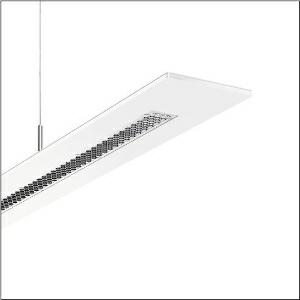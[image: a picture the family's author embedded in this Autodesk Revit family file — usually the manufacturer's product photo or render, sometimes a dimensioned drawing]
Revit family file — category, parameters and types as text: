
# Revit family: arktika_r__21_5mb251dl30830_c5c6
name_source: partatom
category: Lighting Fixtures
units: mm (PartAtom-declared; Revit-internal decimal feet)

## family parameters
Cut with Voids When Loaded = No
Host = Face
Light Source = No
Part Type = Normal
Room Calculation Point = No
Round Connector Dimension = Use Diameter
Shared = No

## types (1)
- --- (1 x LED 3000K / CRI = 80 (unbekannt), 4050 lm, 3000K)
    Apparent Load = 34 VA
    CIE Flux Codes = 81 100 100 79 100
    Color Rendering = 80
    Color Temperature = 3000K
    Default Elevation = 1800 mm
    Description = Arktika® 21, office luminaire, primary anti-glare with honeycomb louvre, of plastic, aluminium vaporised, highly specular, light emission: direct/indirect distribution, primary light characteristic: symmetric, installation type: suspended mounting, LED, rated luminous flux: 4.050lm, luminous efficacy: 120lm/W, light colour: 830, colour temperature: 3000K, control gear: DALI, with terminal, 3+2-pole, max. 2.5mm², mains connection: 220..240V, AC, 50/60Hz, rated input power: 34W, housing, of aluminium, powder-coated, traffic white (RAL 9016), 1-length, length: 1.250mm, width: 120mm, height: 8mm, protection rating (complete): IP20, insulation class (complete): insulation class II (safety insulation), certification: CE, ENEC, VDE, packaging unit: 1 piece
    Height = 8 mm  [stored 0.0262467 ft]
    Lamp = 1 x LED 3000K / CRI >= 80 (unbekannt)
    Lamp Light Flux = 4050 lm
    Lamp count = 1
    Length = 1250 mm
    Luminous efficacy = 120 lm/W
    Manufacturer = Siteco
    ModVariant = No
    Model = 5MB251DL30830
    Mounting Place = Ceiling
    Mounting Type = Pendant
    Number of Poles = 1
    OnlyDefault = Yes
    Power Factor = 1
    Product Name = Arktika® 21
    Product group = office luminaire | ceiling pendant
    ProductGroupID = 903
    Protection Class = Protection class II
    Protection Degree = IP 20
    RLX_Detail_Level = 1
    RLX_Emergency_Light_Flux = 0 lm
    RLX_Emergency_Type = 0
    RLX_Emergency_Type_DB = No
    RlxData = <blob elided: 39321 chars, md5=1d22e380>
    Socket = socket
    Standby Power = 0 W
    System Light Flux = 4050 lm
    System Power = 34 W
    Type Comments = factory setting: luminous flux: 100 % | dim-lin: 254 | 665 mA
    Type Image = l_1006128.jpg
    URL = http://relux.com
    VarID = @adj_219945
    Voltage = 0 V
    Weight = 0.00 kg
    Width = 120 mm

note: [stored X ft] marks values corroborated as IEEE doubles in the binary element streams (Revit-internal decimal feet)

## geometry (parser evidence)
native form markers: Blend x4, Sweep x12
no freeform markers — native parametric forms only
